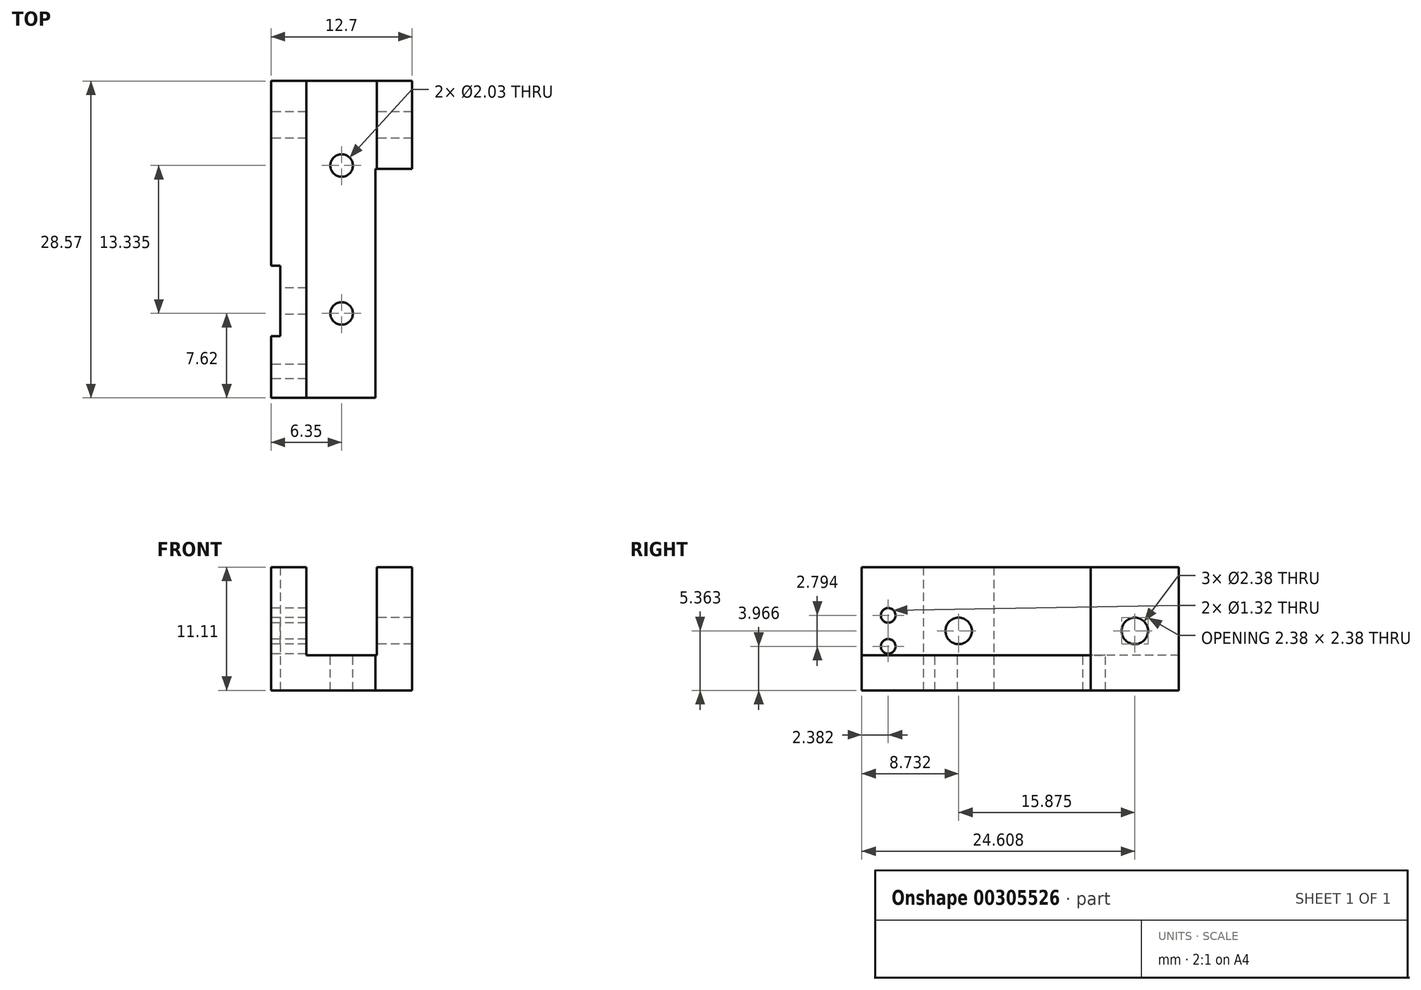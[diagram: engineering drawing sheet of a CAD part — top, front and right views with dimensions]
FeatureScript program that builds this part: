
annotation { "Feature Type Name" : "Feature", "Feature Type Description" : "" }
export const myFeature = defineFeature(function(context is Context, id is Id, definition is map)
    precondition{}
    {
        {
            var Q0;
            Q0=qCreatedBy(makeId("Front.planeOp"),FACE);
            var sketch = newSketch(context, id + "F0", { "sketchPlane" : qUnion([Q0])});
            skLineSegment(sketch, "E0.bottom", {"start": v(0, 0) * mm, "end": v(12.7, 0) * mm});
            skLineSegment(sketch, "E0.top", {"start": v(0, 11.11) * mm, "end": v(3.17, 11.11) * mm});
            skLineSegment(sketch, "E0.left", {"start": v(0, 0) * mm, "end": v(0, 11.11) * mm});
            skLineSegment(sketch, "E0.right", {"start": v(12.7, 0) * mm, "end": v(12.7, 11.11) * mm});
            skLineSegment(sketch, "E1.top", {"start": v(3.18, 3.17) * mm, "end": v(9.53, 3.17) * mm});
            skLineSegment(sketch, "E1.left", {"start": v(3.17, 11.11) * mm, "end": v(3.18, 3.17) * mm});
            skLineSegment(sketch, "E1.right", {"start": v(9.53, 11.11) * mm, "end": v(9.53, 3.17) * mm});
            skLineSegment(sketch, "E2.trimOffspring", {"start": v(9.53, 11.11) * mm, "end": v(12.7, 11.11) * mm});
            skSolve(sketch);
        }
        {
            var Q0;
            Q0 = qSketchRegion(id + "F0", true);
            extrude(context, id + "F1", {"entities" : qUnion([Q0]), "oppositeDirection" : true, "depth" : 28.57 * mm});
        }
        {
            var Q0;
            Q0=qCreatedBy(makeId("Top.planeOp"),FACE);
            var sketch = newSketch(context, id + "F2", { "sketchPlane" : qUnion([Q0])});
            skLineSegment(sketch, "E3.bottom", {"start": v(22.1, -17.46) * mm, "end": v(9.4, -17.46) * mm});
            skLineSegment(sketch, "E3.top", {"start": v(22.1, 20.64) * mm, "end": v(9.4, 20.64) * mm});
            skLineSegment(sketch, "E3.left", {"start": v(22.1, -17.46) * mm, "end": v(22.1, 20.64) * mm});
            skLineSegment(sketch, "E3.right", {"start": v(9.4, -17.46) * mm, "end": v(9.4, 20.64) * mm});
            skSolve(sketch);
        }
        {
            var Q0;
            Q0=makeQuery(id+"F2.imprint","IMPRINT",FACE,{"disambiguationData":[TD([[makeQuery(id+"F2.imprint","IMPRINT",EDGE,{"derivedFrom":sQuery(id+"F2.wireOp",EDGE,"E3.bottom")}),-1.0]])]});
            extrude(context, id + "F3", {"entities" : qUnion([Q0]), "operationType" : NewBodyOperationType.REMOVE, "depth" : 25.4 * mm, "hasSecondDirection" : true, "secondDirectionOppositeDirection" : true, "secondDirectionDepth" : 25.4 * mm});
        }
        {
            var Q0;
            Q0=qCreatedBy(makeId("Right.planeOp"),FACE);
            var sketch = newSketch(context, id + "F4", { "sketchPlane" : qUnion([Q0])});
            skLineSegment(sketch, "E4", {"start": v(0, 0) * mm, "end": v(0, -12.7) * mm});
            skLineSegment(sketch, "E5", {"start": v(0, -12.7) * mm, "end": v(2.38, -12.7) * mm});
            skLineSegment(sketch, "E6", {"start": v(2.38, -12.7) * mm, "end": v(2.38, 3.3) * mm, "construction": true});
            skLineSegment(sketch, "E7", {"start": v(2.38, 25.2) * mm, "end": v(8.73, 25.2) * mm, "construction": true});
            skLineSegment(sketch, "E8", {"start": v(8.73, 25.2) * mm, "end": v(8.73, 6.55) * mm, "construction": true});
            skLineSegment(sketch, "E9", {"start": v(8.73, -12.7) * mm, "end": v(24.6, -12.7) * mm, "construction": true});
            skLineSegment(sketch, "E10", {"start": v(24.6, -12.7) * mm, "end": v(24.6, 4.17) * mm, "construction": true});
            skLineSegment(sketch, "E11", {"start": v(24.6, 25.2) * mm, "end": v(50, 25.2) * mm, "construction": true});
            skLineSegment(sketch, "E12", {"start": v(50, 25.2) * mm, "end": v(50, 5.36) * mm, "construction": true});
            skLineSegment(sketch, "E13", {"start": v(50, 5.36) * mm, "end": v(25.8, 5.36) * mm, "construction": true});
            skLineSegment(sketch, "E14", {"start": v(-26.2, 5.36) * mm, "end": v(-26.2, 3.97) * mm});
            skLineSegment(sketch, "E15", {"start": v(-26.2, 3.97) * mm, "end": v(1.72, 3.97) * mm, "construction": true});
            skCircle(sketch, "E16", {"center": v(8.73, 5.36) * mm, "radius": 1.2 * mm});
            skCircle(sketch, "E17", {"center": v(24.6, 5.36) * mm, "radius": 1.2 * mm});
            skCircle(sketch, "E18", {"center": v(2.38, 3.97) * mm, "radius": 0.66 * mm});
            skCircle(sketch, "E19.MirrorC", {"center": v(2.38, 6.76) * mm, "radius": 0.66 * mm});
            skLineSegment(sketch, "E20.trimOffspring", {"start": v(24.6, 6.55) * mm, "end": v(24.6, 25.2) * mm, "construction": true});
            skLineSegment(sketch, "E21.trimOffspring", {"start": v(23.42, 5.36) * mm, "end": v(9.92, 5.36) * mm, "construction": true});
            skLineSegment(sketch, "E22.trimOffspring", {"start": v(7.54, 5.36) * mm, "end": v(-26.2, 5.36) * mm, "construction": true});
            skLineSegment(sketch, "E23.trimOffspring", {"start": v(8.73, 4.17) * mm, "end": v(8.73, -12.7) * mm, "construction": true});
            skLineSegment(sketch, "E24.trimOffspring", {"start": v(3.04, 3.97) * mm, "end": v(3.79, 3.97) * mm});
            skLineSegment(sketch, "E25.trimOffspring", {"start": v(2.38, 4.63) * mm, "end": v(2.38, 6.1) * mm});
            skLineSegment(sketch, "E26.trimOffspring", {"start": v(2.38, 7.42) * mm, "end": v(2.38, 25.2) * mm, "construction": true});
            skSolve(sketch);
        }
        {
            var Q0;
            Q0 = qSketchRegion(id + "F4", true);
            extrude(context, id + "F5", {"entities" : qUnion([Q0]), "operationType" : NewBodyOperationType.REMOVE, "depth" : 25.4 * mm, "hasSecondDirection" : true, "secondDirectionOppositeDirection" : true, "secondDirectionDepth" : 25.4 * mm});
        }
        {
            var Q0;
            Q0=qCreatedBy(makeId("Right.planeOp"),FACE);
            var sketch = newSketch(context, id + "F6", { "sketchPlane" : qUnion([Q0])});
            skLineSegment(sketch, "E27.bottom", {"start": v(11.9, 22.74) * mm, "end": v(5.56, 22.74) * mm});
            skLineSegment(sketch, "E27.top", {"start": v(11.9, -2.66) * mm, "end": v(5.56, -2.66) * mm});
            skLineSegment(sketch, "E27.left", {"start": v(11.9, 22.74) * mm, "end": v(11.9, -2.66) * mm});
            skLineSegment(sketch, "E27.right", {"start": v(5.56, 22.74) * mm, "end": v(5.56, -2.66) * mm});
            skSolve(sketch);
        }
        {
            var Q0;
            Q0=makeQuery(id+"F6.imprint","IMPRINT",FACE,{"disambiguationData":[TD([[makeQuery(id+"F6.imprint","IMPRINT",EDGE,{"derivedFrom":sQuery(id+"F6.wireOp",EDGE,"E27.bottom")}),1.0]])]});
            extrude(context, id + "F7", {"entities" : qUnion([Q0]), "operationType" : NewBodyOperationType.REMOVE, "depth" : 0.81 * mm});
        }
        {
            var Q0;
            Q0=qCreatedBy(makeId("Top.planeOp"),FACE);
            var sketch = newSketch(context, id + "F8", { "sketchPlane" : qUnion([Q0])});
            skLineSegment(sketch, "E28", {"start": v(0, 0) * mm, "end": v(6.35, 0) * mm, "construction": true});
            skLineSegment(sketch, "E29", {"start": v(6.35, 0) * mm, "end": v(6.35, 7.62) * mm, "construction": true});
            skLineSegment(sketch, "E30", {"start": v(0, 0) * mm, "end": v(0, 28.58) * mm, "construction": true});
            skLineSegment(sketch, "E31", {"start": v(0, 28.58) * mm, "end": v(6.35, 28.58) * mm, "construction": true});
            skLineSegment(sketch, "E32", {"start": v(6.35, 28.58) * mm, "end": v(6.35, 20.96) * mm, "construction": true});
            skCircle(sketch, "E33", {"center": v(6.35, 20.96) * mm, "radius": 1.02 * mm});
            skCircle(sketch, "E34", {"center": v(6.35, 7.62) * mm, "radius": 1.02 * mm});
            skSolve(sketch);
        }
        {
            var Q0;
            Q0 = qSketchRegion(id + "F8", true);
            extrude(context, id + "F9", {"entities" : qUnion([Q0]), "operationType" : NewBodyOperationType.REMOVE, "oppositeDirection" : true, "depth" : 25.4 * mm, "hasSecondDirection" : true, "secondDirectionOppositeDirection" : false, "secondDirectionDepth" : 25.4 * mm});
        }
    });
